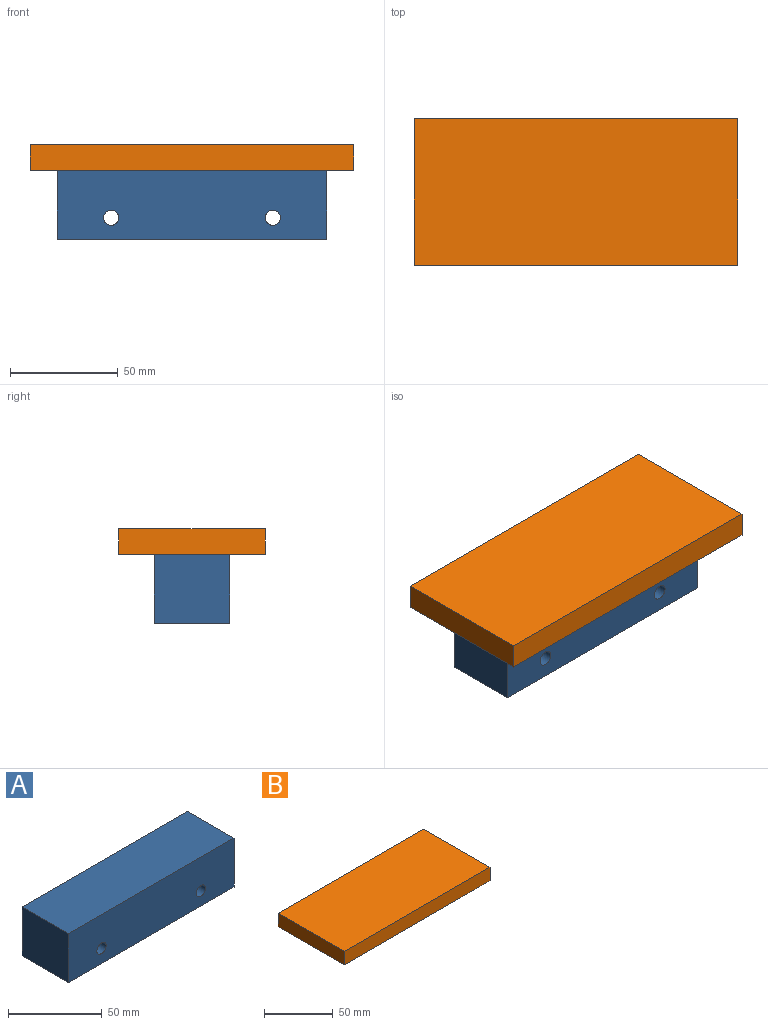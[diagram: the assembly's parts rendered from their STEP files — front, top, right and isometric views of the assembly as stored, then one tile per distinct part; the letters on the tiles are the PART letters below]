
ASSEMBLY  parts=2 mates=1
PART A: 8 faces, bbox 125x35x32 mm
  f0: plane 125x35mm, normal (0,0,1), area 4375mm2, adj f1,f5,f6,f7
  f1: plane 35x32mm, normal (-1,0,0), area 1120mm2, adj f0,f2,f6,f7
  f2: plane 125x35mm, normal (0,0,-1), area 4375mm2, adj f1,f5,f6,f7
  f3: cylinder r=3.5mm len=35mm, axis (0,1,0), area 769.7mm2, adj f6,f7
  f4: cylinder r=3.5mm len=35mm, axis (0,1,0), area 769.7mm2, adj f6,f7
  f5: plane 35x32mm, normal (1,0,0), area 1120mm2, adj f0,f2,f6,f7
  f6: plane 125x32mm, normal (0,-1,0), area 3923mm2, adj f0,f1,f2,f3,f4,f5
  f7: plane 125x32mm, normal (0,1,0), area 3923mm2, adj f0,f1,f2,f3,f4,f5
PART B: 6 faces, bbox 150x68x12 mm
  f0: plane 68x12mm, normal (-1,0,0), area 816mm2, adj f1,f3,f4,f5
  f1: plane 150x12mm, normal (0,-1,0), area 1800mm2, adj f0,f2,f4,f5
  f2: plane 68x12mm, normal (1,0,0), area 816mm2, adj f1,f3,f4,f5
  f3: plane 150x12mm, normal (0,1,0), area 1800mm2, adj f0,f2,f4,f5
  f4: plane 150x68mm, normal (0,0,1), area 10200mm2, adj f0,f1,f2,f3
  f5: plane 150x68mm, normal (0,0,-1), area 10200mm2, adj f0,f1,f2,f3
PLACE A t=(7.47,6.44,15.07)mm fixed
PLACE B t=(-130.03,-45.06,47.07)mm
MATE fastened A.f0 <-> B.f5  axis (0,0,1) through (-55.03,-11.06,47.07)mm
